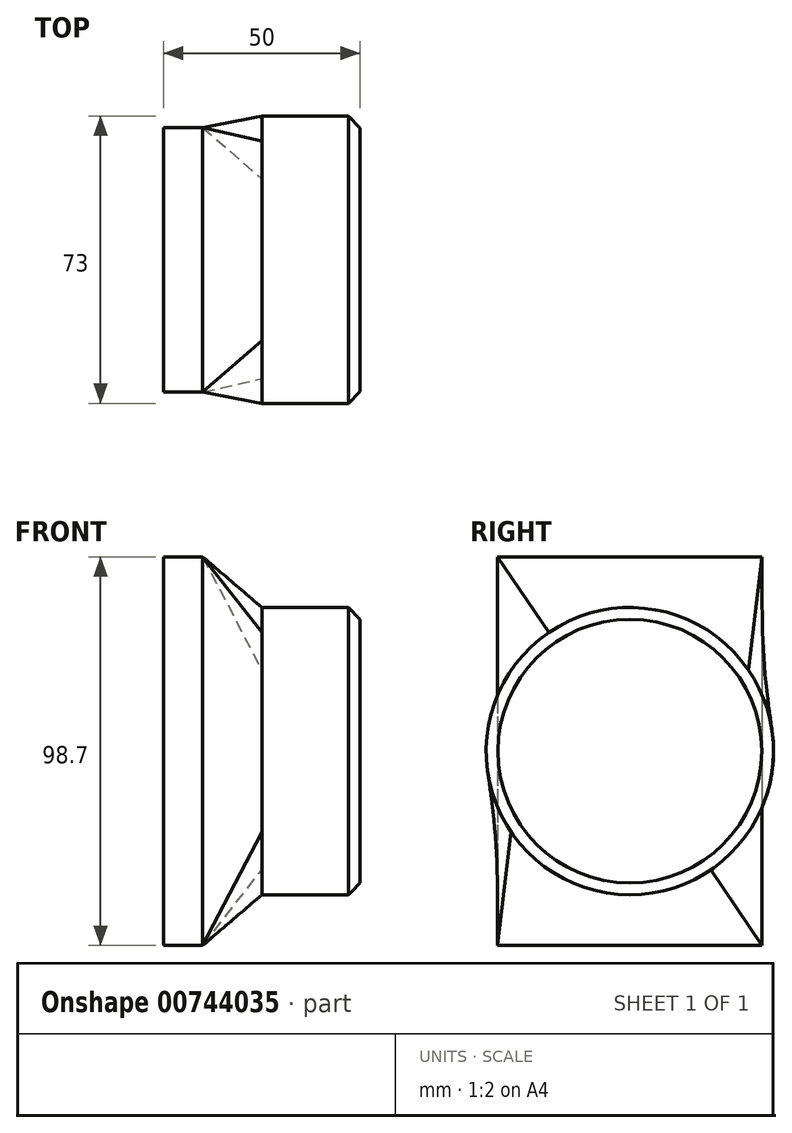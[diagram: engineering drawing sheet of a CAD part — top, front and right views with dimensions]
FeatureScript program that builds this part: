
annotation { "Feature Type Name" : "Feature", "Feature Type Description" : "" }
export const myFeature = defineFeature(function(context is Context, id is Id, definition is map)
    precondition{}
    {
        {
            var Q0;
            Q0=qCreatedBy(makeId("Right.planeOp"),FACE);
            var sketch = newSketch(context, id + "F0", { "sketchPlane" : qUnion([Q0])});
            skCircle(sketch, "E0", {"center": v(0, 0) * mm, "radius": 36.5 * mm});
            skSolve(sketch);
        }
        {
            var Q0;
            Q0 = qSketchRegion(id + "F0", true);
            extrude(context, id + "F1", {"entities" : qUnion([Q0]), "depth" : 25 * mm, "offsetDistance" : 25 * mm});
        }
        {
            var Q0;
            Q0=makeQuery(id+"F1.opExtrude","CAP_FACE",FACE,{"disambiguationData":[OSD([sQuery(id+"F0.wireOp",EDGE,"E0")])],"isStart":true});
            cPlane(context, id + "F2", {"entities" : qUnion([Q0]), "cplaneType" : CPlaneType.OFFSET, "offset" : 25 * mm, "width" : 150 * mm, "height" : 150 * mm});
        }
        {
            var Q0;
            Q0=qCreatedBy(id+"F2.planeOp",FACE);
            var sketch = newSketch(context, id + "F3", { "sketchPlane" : qUnion([Q0])});
            skLineSegment(sketch, "E1.bottom", {"start": v(33.6, 49.35) * mm, "end": v(-33.6, 49.35) * mm});
            skLineSegment(sketch, "E1.top", {"start": v(33.6, -49.35) * mm, "end": v(-33.6, -49.35) * mm});
            skLineSegment(sketch, "E1.left", {"start": v(33.6, 49.35) * mm, "end": v(33.6, -49.35) * mm});
            skLineSegment(sketch, "E1.right", {"start": v(-33.6, 49.35) * mm, "end": v(-33.6, -49.35) * mm});
            skPoint(sketch, "E1.middle", {"position": v(0, 0) * mm});
            skSolve(sketch);
        }
        {
            var Q0;
            Q0 = qSketchRegion(id + "F3", true);
            extrude(context, id + "F4", {"entities" : qUnion([Q0]), "oppositeDirection" : true, "depth" : 10 * mm, "offsetDistance" : 25 * mm});
        }
        {
            var Q1;
            Q1=makeQuery(id+"F4.opExtrude","CAP_FACE",FACE,{"disambiguationData":[OSD([sQuery(id+"F3.wireOp",EDGE,"E1.bottom"),sQuery(id+"F3.wireOp",EDGE,"E1.top"),sQuery(id+"F3.wireOp",EDGE,"E1.left"),sQuery(id+"F3.wireOp",EDGE,"E1.right")])],"isStart":false});
            var Q2;
            Q2=makeQuery(id+"F1.opExtrude","CAP_FACE",FACE,{"disambiguationData":[OSD([sQuery(id+"F0.wireOp",EDGE,"E0")])],"isStart":true});
            loft(context, id + "F5", {"operationType" : NewBodyOperationType.ADD, "sheetProfilesArray" : [{ "sheetProfileEntities" : qUnion([Q1]) }, { "sheetProfileEntities" : qUnion([Q2]) }]});
        }
        {
            var Q0;
            Q0=makeQuery(id+"F1.opExtrude","CAP_EDGE",EDGE,{"disambiguationData":[OSD([sQuery(id+"F0.wireOp",EDGE,"E0")])],"isStart":false});
            chamfer(context, id + "F6", {"entities" : qUnion([Q0]), "width" : 3 * mm, "tangentPropagation" : true});
        }
    });
